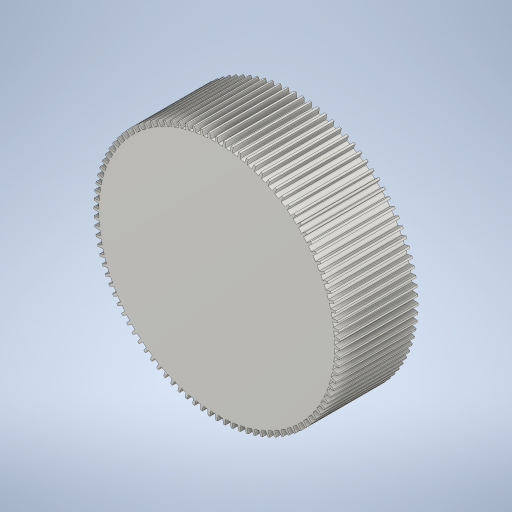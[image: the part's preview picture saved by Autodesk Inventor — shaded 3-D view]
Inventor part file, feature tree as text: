
AUTODESK INVENTOR PART (.ipt)
format: ipt  version: 2024.2 (Build 282272000, 272)  size: 767,488 bytes
history: native  units: mm (DEFAULTED — no unit token found)
features: plane x3, other x3, extrude x2, sketch x2
ambient origin geometry x8: Origin, YZ Plane, XZ Plane, XY Plane, X Axis, Y Axis, Z Axis, Center Point
bodies: Solid1 (feature_tree)
feature tree (10):
  extrude  "Extrusion1"  Depth=16.0mm TaperAngle=0.0deg
  plane  "Work Plane2"
  plane  "Work Plane8"
  plane  "Work Plane9"
  other  "Цилиндрическое зубчатое зацепление"
  extrude  "Выдавливание2"  Depth=10.0mm
  sketch  "Sketch1"  dims[d0=50.0mm d1=16.0mm d2=0.0mm d3=46.0mm d4=10.0mm d5=0.0mm d16=3.65mm d17=0.0mm d34=0.314159mm d39=0.0mm d41=0.0mm d43=3.65mm d46=3.65mm d47=0.0mm d48=0.0mm d49=48.0mm d50=0.0mm d51=0.0mm]
  other  "Srf1"
  sketch  "Эскиз3"
  other  "Средний диаметр"
